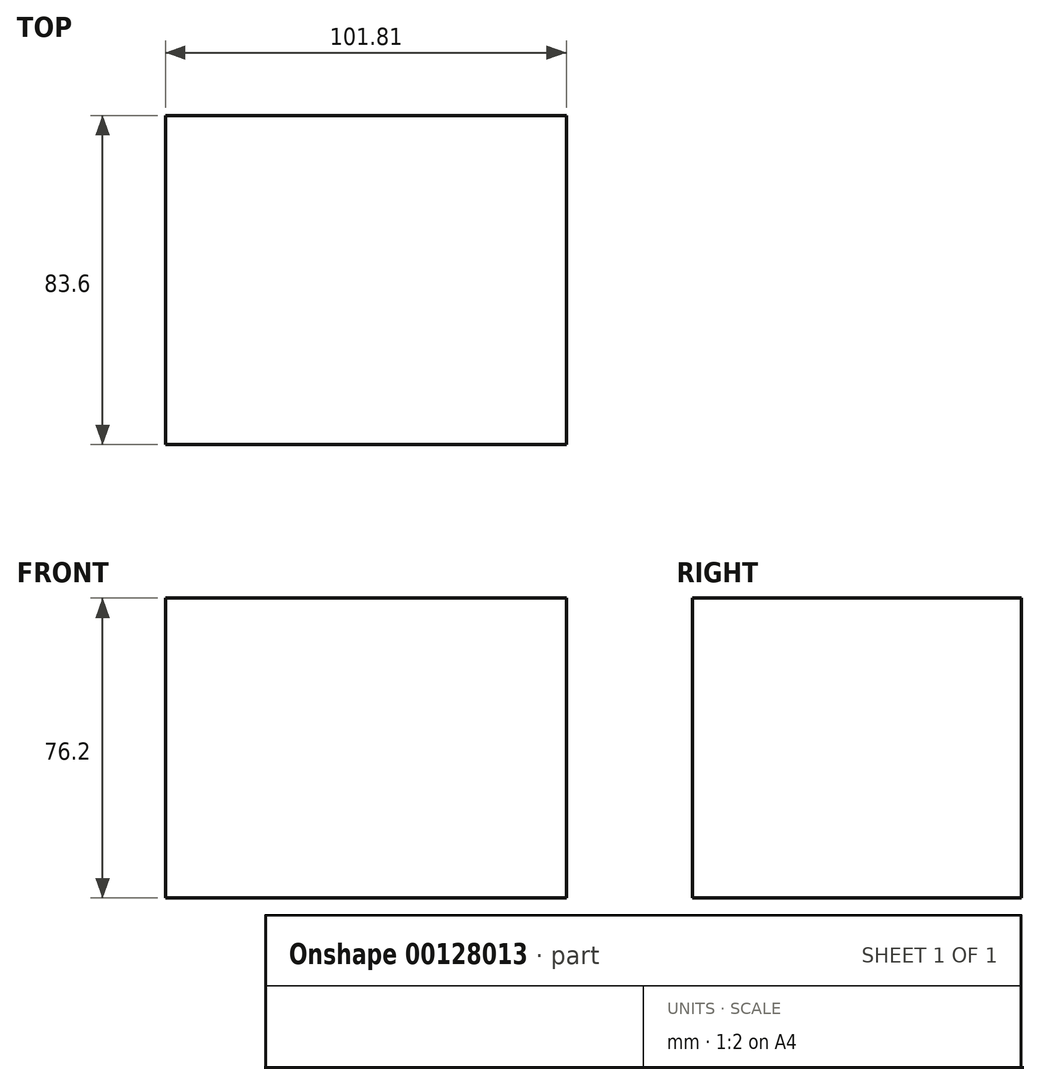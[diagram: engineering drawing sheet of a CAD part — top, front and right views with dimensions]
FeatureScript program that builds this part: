
annotation { "Feature Type Name" : "Feature", "Feature Type Description" : "" }
export const myFeature = defineFeature(function(context is Context, id is Id, definition is map)
    precondition{}
    {
        {
            var Q0;
            Q0=qCreatedBy(makeId("Top.planeOp"),FACE);
            var sketch = newSketch(context, id + "F0", { "sketchPlane" : qUnion([Q0])});
            skLineSegment(sketch, "E0.bottom", {"start": v(-47.44, 42.83) * mm, "end": v(54.37, 42.83) * mm});
            skLineSegment(sketch, "E0.top", {"start": v(-47.44, -40.77) * mm, "end": v(54.37, -40.77) * mm});
            skLineSegment(sketch, "E0.left", {"start": v(-47.44, 42.83) * mm, "end": v(-47.44, -40.77) * mm});
            skLineSegment(sketch, "E0.right", {"start": v(54.37, 42.83) * mm, "end": v(54.37, -40.77) * mm});
            skSolve(sketch);
        }
        {
            var Q0;
            Q0 = qSketchRegion(id + "F0", true);
            extrude(context, id + "F1", {"entities" : qUnion([Q0]), "depth" : 76.2 * mm});
        }
        {
            var Q0;
            Q0=makeQuery(id+"F1.opExtrude","CAP_FACE",FACE,{"disambiguationData":[OSD([sQuery(id+"F0.wireOp",EDGE,"E0.bottom"),sQuery(id+"F0.wireOp",EDGE,"E0.top"),sQuery(id+"F0.wireOp",EDGE,"E0.left"),sQuery(id+"F0.wireOp",EDGE,"E0.right")])],"isStart":false});
            var sketch = newSketch(context, id + "F2", { "sketchPlane" : qUnion([Q0])});
            skSolve(sketch);
        }
        {
            var Q0;
            Q0=makeQuery(id+"F2.imprint","IMPRINT",FACE,{"disambiguationData":[TD([[makeQuery(id+"F2.imprint","IMPRINT",EDGE,{"derivedFrom":makeQuery(id+"F1.opExtrude","CAP_EDGE",EDGE,{"disambiguationData":[OSD([sQuery(id+"F0.wireOp",EDGE,"E0.bottom")])],"isStart":false})}),-1.0]])]});
            var sketch = newSketch(context, id + "F3", { "sketchPlane" : qUnion([Q0])});
            skCircle(sketch, "E1", {"center": v(-22.61, 12.94) * mm, "radius": 13.03 * mm});
            skSolve(sketch);
        }
        {
            var Q0;
            Q0 = qSketchRegion(id + "F3", true);
            var Q1;
            Q1=makeQuery(id+"F2.imprint","IMPRINT",FACE,{"disambiguationData":[TD([[makeQuery(id+"F2.imprint","IMPRINT",EDGE,{"derivedFrom":makeQuery(id+"F1.opExtrude","CAP_EDGE",EDGE,{"disambiguationData":[OSD([sQuery(id+"F0.wireOp",EDGE,"E0.bottom")])],"isStart":false})}),-1.0]])]});
            extrude(context, id + "F4", {"entities" : qUnion([Q0, Q1]), "operationType" : NewBodyOperationType.REMOVE, "endBound" : BoundingType.THROUGH_ALL, "oppositeDirection" : true, "depth" : 23.44 * mm});
        }
        {
            var Q0;
            Q0 = qSketchRegion(id + "F0", true);
            extrude(context, id + "F5", {"entities" : qUnion([Q0]), "oppositeDirection" : true, "depth" : 76.2 * mm});
        }
    });
